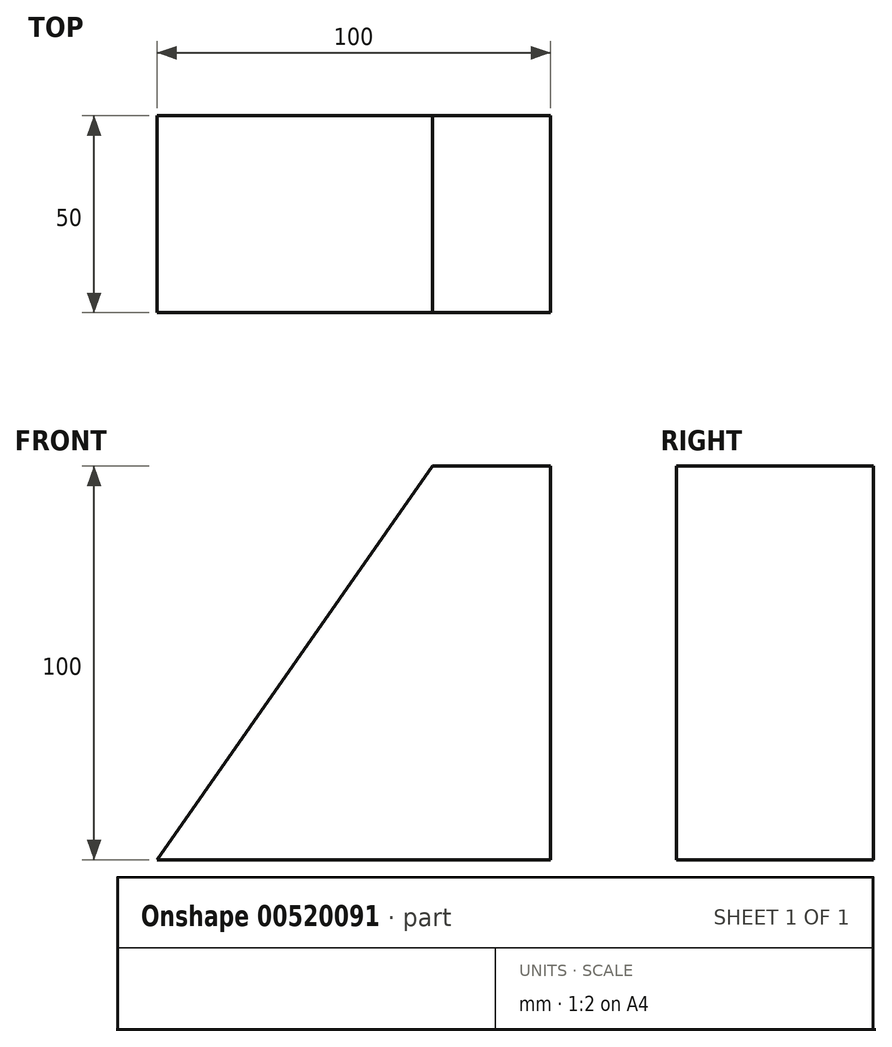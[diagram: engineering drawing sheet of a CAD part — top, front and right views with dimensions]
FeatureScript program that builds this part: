
annotation { "Feature Type Name" : "Feature", "Feature Type Description" : "" }
export const myFeature = defineFeature(function(context is Context, id is Id, definition is map)
    precondition{}
    {
        {
            var Q0;
            Q0=qCreatedBy(makeId("Front.planeOp"),FACE);
            var sketch = newSketch(context, id + "F0", { "sketchPlane" : qUnion([Q0])});
            skLineSegment(sketch, "E0", {"start": v(0, 0) * mm, "end": v(-100, 0) * mm});
            skLineSegment(sketch, "E1", {"start": v(0, 0) * mm, "end": v(0, 100) * mm});
            skLineSegment(sketch, "E2", {"start": v(0, 100) * mm, "end": v(-100, 100) * mm});
            skLineSegment(sketch, "E3", {"start": v(-100, 100) * mm, "end": v(-100, 0) * mm});
            skSolve(sketch);
        }
        {
            var Q0;
            Q0=makeQuery(id+"F0.imprint","IMPRINT",FACE,{"disambiguationData":[TD([[makeQuery(id+"F0.imprint","IMPRINT",EDGE,{"derivedFrom":sQuery(id+"F0.wireOp",EDGE,"E0")}),-1.0]])]});
            extrude(context, id + "F1", {"entities" : qUnion([Q0]), "depth" : 50 * mm, "offsetDistance" : 25 * mm});
        }
        {
            var Q0;
            Q0=makeQuery(id+"F1.opExtrude","SWEPT_EDGE",EDGE,{"disambiguationData":[OSD([sQuery(id+"F0.wireOp",EDGE,"E2"),sQuery(id+"F0.wireOp",EDGE,"E3")])]});
            chamfer(context, id + "F2", {"entities" : qUnion([Q0]), "chamferType" : ChamferType.TWO_OFFSETS, "width1" : 100 * mm, "oppositeDirection" : false, "width2" : 70 * mm, "tangentPropagation" : true});
        }
    });
